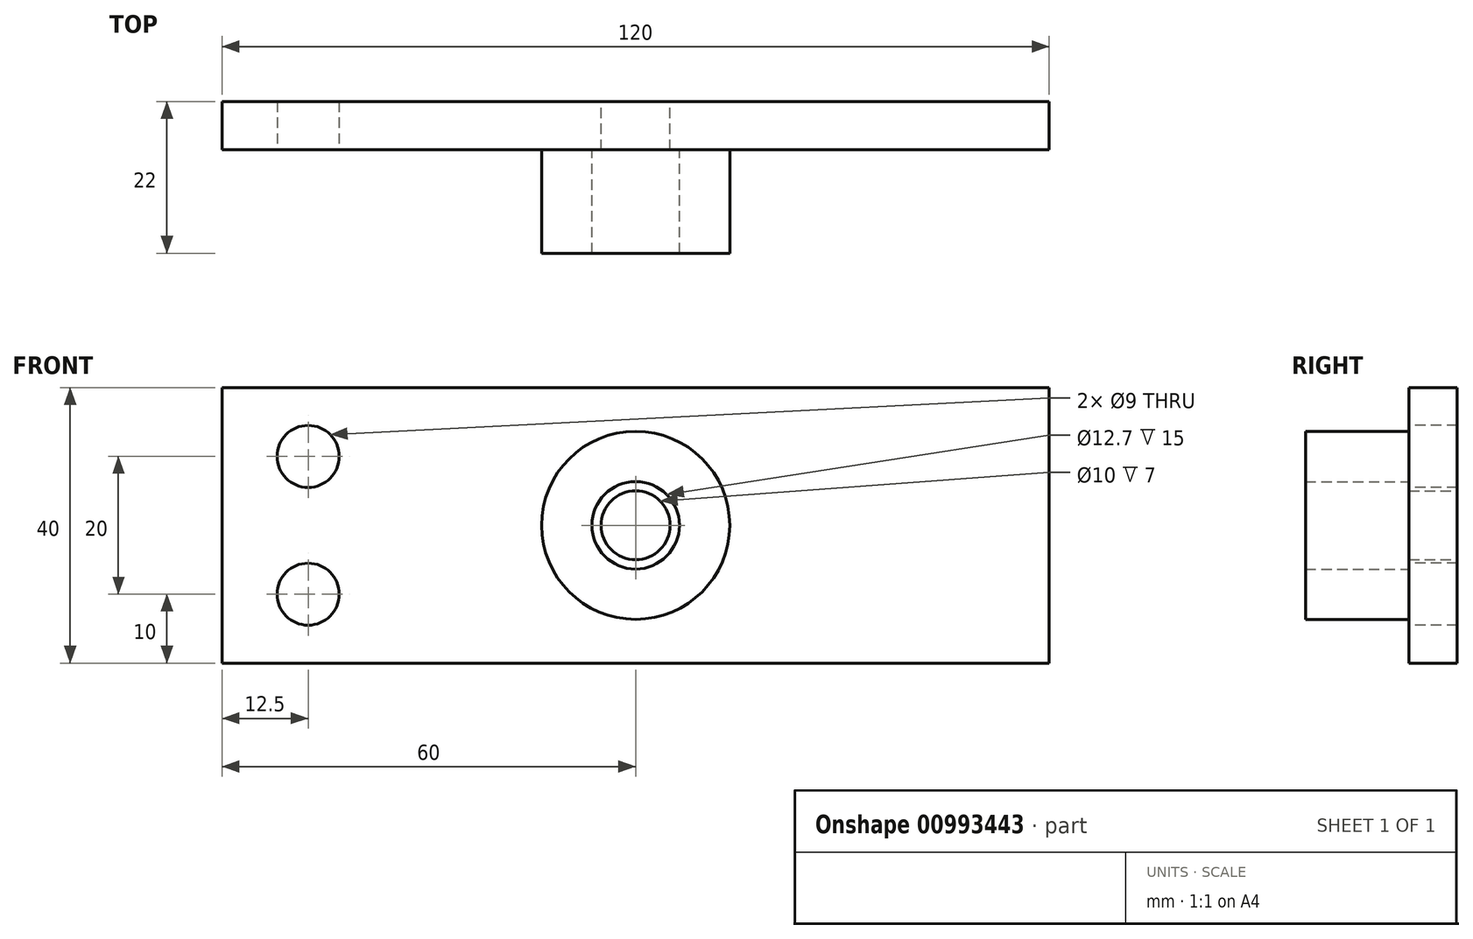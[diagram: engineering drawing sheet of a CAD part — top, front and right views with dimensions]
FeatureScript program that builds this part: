
annotation { "Feature Type Name" : "Feature", "Feature Type Description" : "" }
export const myFeature = defineFeature(function(context is Context, id is Id, definition is map)
    precondition{}
    {
        {
            var Q0;
            Q0=qCreatedBy(makeId("Front.planeOp"),FACE);
            var sketch = newSketch(context, id + "F0", { "sketchPlane" : qUnion([Q0])});
            skCircle(sketch, "E0", {"center": v(0, 0) * mm, "radius": 6.35 * mm});
            skCircle(sketch, "E1.0", {"center": v(0, 0) * mm, "radius": 13.65 * mm});
            skSolve(sketch);
        }
        {
            var Q0;
            Q0 = qSketchRegion(id + "F0", true);
            extrude(context, id + "F1", {"entities" : qUnion([Q0]), "depth" : 15 * mm, "offsetDistance" : 25 * mm});
        }
        {
            var Q0;
            Q0=qCreatedBy(makeId("Front.planeOp"),FACE);
            var sketch = newSketch(context, id + "F2", { "sketchPlane" : qUnion([Q0])});
            skLineSegment(sketch, "E2.bottom", {"start": v(-60, -20) * mm, "end": v(60, -20) * mm});
            skLineSegment(sketch, "E2.top", {"start": v(-60, 20) * mm, "end": v(60, 20) * mm});
            skLineSegment(sketch, "E2.left", {"start": v(-60, -20) * mm, "end": v(-60, 20) * mm});
            skLineSegment(sketch, "E2.right", {"start": v(60, -20) * mm, "end": v(60, 20) * mm});
            skPoint(sketch, "E2.middle", {"position": v(0, 0) * mm});
            skSolve(sketch);
        }
        {
            var Q0;
            Q0 = qSketchRegion(id + "F2", true);
            extrude(context, id + "F3", {"entities" : qUnion([Q0]), "operationType" : NewBodyOperationType.ADD, "oppositeDirection" : true, "depth" : 7 * mm, "offsetDistance" : 25 * mm});
        }
        {
            var Q0;
            {var subQ0=sQuery(id+"F2.wireOp",EDGE,"E2.left");var subQ1=sQuery(id+"F2.wireOp",EDGE,"E2.top");var subQ2=sQuery(id+"F2.wireOp",EDGE,"E2.bottom");var subQ3=sQuery(id+"F2.wireOp",EDGE,"E2.right");Q0=makeQuery(id+"F3.boolean.opBoolean","SPLIT",FACE,{"disambiguationData":[TD([makeQuery(id+"F1.opExtrude","SWEPT_FACE",FACE,{"disambiguationData":[OSD([sQuery(id+"F0.wireOp",EDGE,"E1.0")])]})])],"derivedFrom":makeQuery(id+"F3.opExtrude","CAP_FACE",FACE,{"disambiguationData":[OSD([subQ2,subQ1,subQ0,subQ3])],"isStart":true})});}
            var sketch = newSketch(context, id + "F4", { "sketchPlane" : qUnion([Q0])});
            skPoint(sketch, "E3", {"position": v(-47.5, 10) * mm});
            skPoint(sketch, "E4", {"position": v(-47.5, -10) * mm});
            skSolve(sketch);
        }
        {
            var Q0;
            Q0=sQuery(id+"F4.wireOp",VERTEX,"E3");
            var Q1;
            Q1=sQuery(id+"F4.wireOp",VERTEX,"E4");
            var Q2;
            Q2=makeQuery(id+"F1.opExtrude","SWEPT_BODY",BODY,{"disambiguationData":[OSD([sQuery(id+"F0.wireOp",EDGE,"E0"),sQuery(id+"F0.wireOp",EDGE,"E1.0")])]});
            hole(context, id + "F5", {"style" : HoleStyle.SIMPLE, "endStyle" : HoleEndStyle.THROUGH, "standardTappedOrClearance" : lookupTablePath({ "fit" : "Normal", "standard" : "ISO", "size" : "M8", "type" : "Clearance" }), "standardBlindInLast" : lookupTablePath({ "fit" : "Normal", "standard" : "ISO", "engagement" : "75%", "pitch" : "1.25 mm", "size" : "M8", "type" : "Clearance & tapped" }), "holeDiameter" : 9 * mm, "majorDiameter" : 5 * mm, "isTappedThrough" : true, "tappedDepth" : 12 * mm, "tapClearance" : 3, "locations" : qUnion([Q0, Q1]), "scope" : qUnion([Q2])});
        }
        {
            var Q0;
            Q0=makeQuery(id+"F3.opExtrude","CAP_FACE",FACE,{"disambiguationData":[OSD([sQuery(id+"F2.wireOp",EDGE,"E2.bottom"),sQuery(id+"F2.wireOp",EDGE,"E2.top"),sQuery(id+"F2.wireOp",EDGE,"E2.left"),sQuery(id+"F2.wireOp",EDGE,"E2.right")])],"isStart":false});
            var sketch = newSketch(context, id + "F6", { "sketchPlane" : qUnion([Q0])});
            skPoint(sketch, "E5", {"position": v(0, 0) * mm});
            skSolve(sketch);
        }
        {
            var Q0;
            Q0=sQuery(id+"F6.wireOp",VERTEX,"E5");
            var Q1;
            Q1=makeQuery(id+"F1.opExtrude","SWEPT_BODY",BODY,{"disambiguationData":[OSD([sQuery(id+"F0.wireOp",EDGE,"E0"),sQuery(id+"F0.wireOp",EDGE,"E1.0")])]});
            hole(context, id + "F7", {"style" : HoleStyle.SIMPLE, "endStyle" : HoleEndStyle.BLIND, "holeDiameter" : 10 * mm, "majorDiameter" : 5 * mm, "holeDepth" : 100 * mm, "isTappedThrough" : true, "tappedDepth" : 12 * mm, "tapClearance" : 3, "locations" : qUnion([Q0]), "scope" : qUnion([Q1])});
        }
    });
